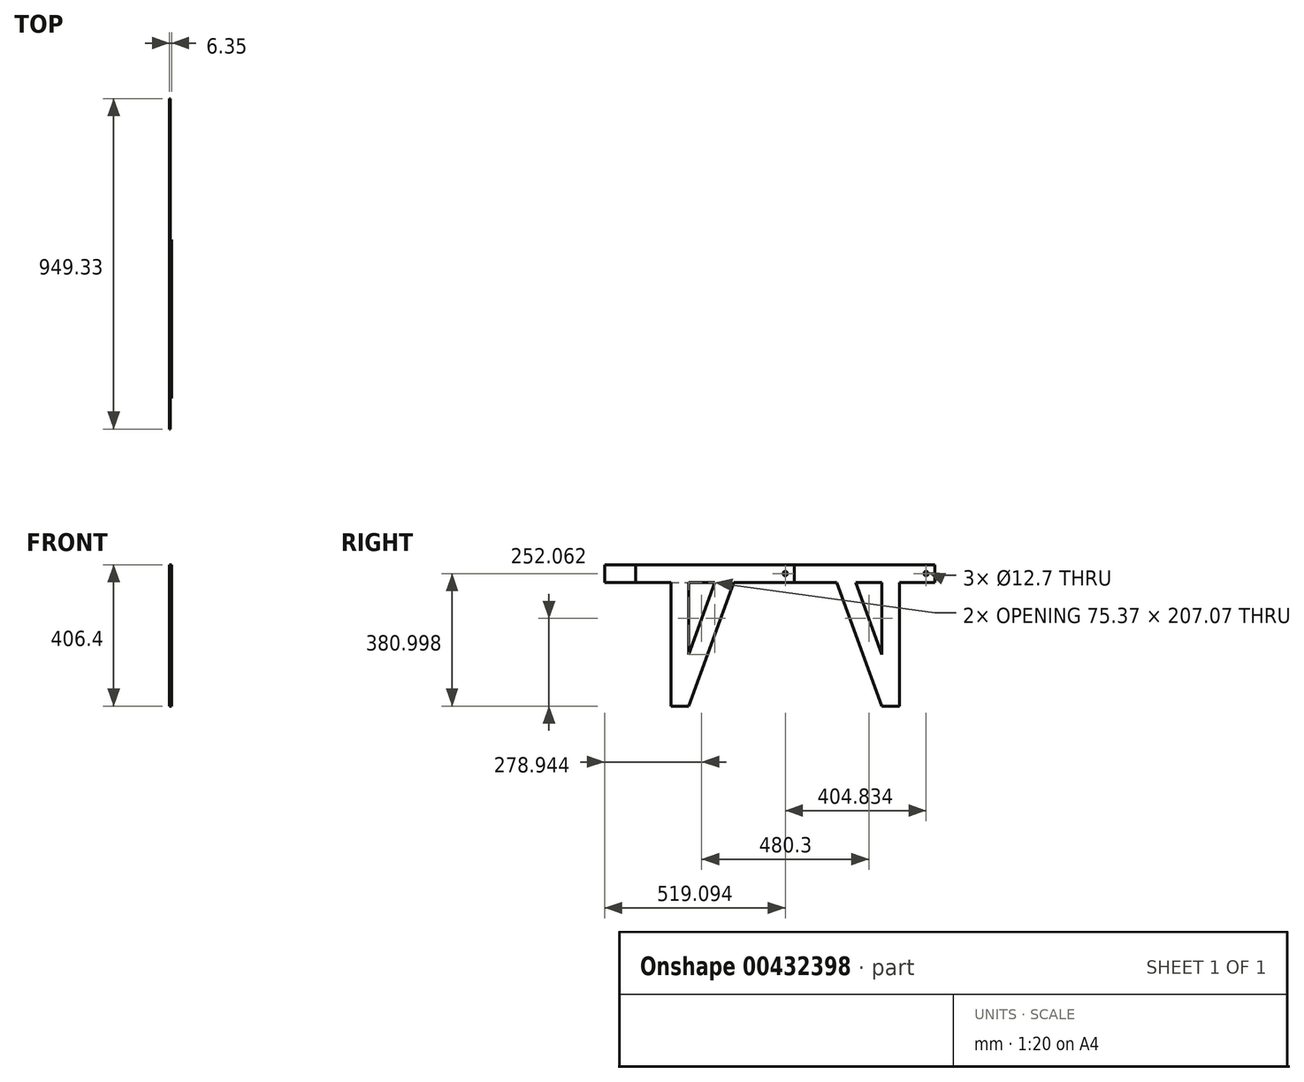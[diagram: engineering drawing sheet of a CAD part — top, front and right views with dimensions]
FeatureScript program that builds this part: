
annotation { "Feature Type Name" : "Feature", "Feature Type Description" : "" }
export const myFeature = defineFeature(function(context is Context, id is Id, definition is map)
    precondition{}
    {
        {
            var Q0;
            Q0=qCreatedBy(makeId("Right.planeOp"),FACE);
            var sketch = newSketch(context, id + "F0", { "sketchPlane" : qUnion([Q0])});
            skLineSegment(sketch, "E0.bottom", {"start": v(-588.96, 209.37) * mm, "end": v(360.37, 209.37) * mm});
            skLineSegment(sketch, "E0.top", {"start": v(-588.96, 158.57) * mm, "end": v(78.54, 158.57) * mm});
            skLineSegment(sketch, "E0.left", {"start": v(-588.96, 209.37) * mm, "end": v(-588.96, 158.57) * mm});
            skLineSegment(sketch, "E0.right", {"start": v(360.37, 209.37) * mm, "end": v(360.37, 158.57) * mm});
            skLineSegment(sketch, "E1.top", {"start": v(207.97, -197.03) * mm, "end": v(258.77, -197.03) * mm});
            skLineSegment(sketch, "E1.left", {"start": v(207.97, 158.57) * mm, "end": v(207.97, -48.5) * mm});
            skLineSegment(sketch, "E1.right", {"start": v(258.77, 158.57) * mm, "end": v(258.77, -197.03) * mm});
            skLineSegment(sketch, "E2.left", {"start": v(78.54, 158.57) * mm, "end": v(207.97, -197.03) * mm});
            skLineSegment(sketch, "E2.right", {"start": v(132.6, 158.57) * mm, "end": v(207.97, -48.5) * mm});
            skLineSegment(sketch, "E3.trimOffspring", {"start": v(132.6, 158.57) * mm, "end": v(207.97, 158.57) * mm});
            skLineSegment(sketch, "E4.trimOffspring", {"start": v(258.77, 158.57) * mm, "end": v(360.37, 158.57) * mm});
            skLineSegment(sketch, "E5", {"start": v(132.6, 158.57) * mm, "end": v(84.86, 141.2) * mm, "construction": true});
            skLineSegment(sketch, "E6", {"start": v(233.37, -197.03) * mm, "end": v(233.37, 183.97) * mm, "construction": true});
            skLineSegment(sketch, "E7", {"start": v(233.37, 183.97) * mm, "end": v(360.37, 183.97) * mm, "construction": true});
            skCircle(sketch, "E8", {"center": v(334.97, 183.97) * mm, "radius": 6.35 * mm});
            skSolve(sketch);
        }
        {
            var Q0;
            Q0=qSketchRegion(id+"F0",true);
            extrude(context, id + "F1", {"entities" : qUnion([Q0]), "depth" : 3.17 * mm});
        }
        {
            var Q0;
            Q0=makeQuery(id+"F1.opExtrude","CAP_FACE",FACE,{"disambiguationData":[OSD([sQuery(id+"F0.wireOp",EDGE,"E0.bottom"),sQuery(id+"F0.wireOp",EDGE,"E0.top"),sQuery(id+"F0.wireOp",EDGE,"E0.left"),sQuery(id+"F0.wireOp",EDGE,"E0.right"),sQuery(id+"F0.wireOp",EDGE,"E1.top"),sQuery(id+"F0.wireOp",EDGE,"E1.left"),sQuery(id+"F0.wireOp",EDGE,"E1.right"),sQuery(id+"F0.wireOp",EDGE,"E2.left"),sQuery(id+"F0.wireOp",EDGE,"E2.right"),sQuery(id+"F0.wireOp",EDGE,"E3.trimOffspring"),sQuery(id+"F0.wireOp",EDGE,"238dff0e-271b-4be5-b624-802031fdb64e.trimOffspring"),sQuery(id+"F0.wireOp",EDGE,"E4.trimOffspring"),sQuery(id+"F0.wireOp",EDGE,"E8")])],"isStart":false});
            var sketch = newSketch(context, id + "F2", { "sketchPlane" : qUnion([Q0])});
            skLineSegment(sketch, "E9", {"start": v(-347.7, -197.03) * mm, "end": v(-398.5, -197.03) * mm});
            skLineSegment(sketch, "E10", {"start": v(-398.5, -197.03) * mm, "end": v(-398.5, 158.57) * mm});
            skLineSegment(sketch, "E11", {"start": v(-398.5, 158.57) * mm, "end": v(-500.1, 158.57) * mm});
            skLineSegment(sketch, "E12", {"start": v(-500.1, 158.57) * mm, "end": v(-500.1, 209.37) * mm});
            skLineSegment(sketch, "E13", {"start": v(-500.1, 209.37) * mm, "end": v(-44.47, 209.37) * mm});
            skLineSegment(sketch, "E14", {"start": v(-44.47, 209.37) * mm, "end": v(-44.47, 158.57) * mm});
            skLineSegment(sketch, "E15", {"start": v(-44.47, 158.57) * mm, "end": v(-218.27, 158.57) * mm});
            skLineSegment(sketch, "E16", {"start": v(-218.27, 158.57) * mm, "end": v(-347.7, -197.03) * mm});
            skLineSegment(sketch, "E17", {"start": v(-347.7, -48.5) * mm, "end": v(-272.33, 158.57) * mm});
            skLineSegment(sketch, "E18", {"start": v(-272.33, 158.57) * mm, "end": v(-347.7, 158.57) * mm});
            skLineSegment(sketch, "E19", {"start": v(-347.7, 158.57) * mm, "end": v(-347.7, -48.5) * mm});
            skLineSegment(sketch, "E20", {"start": v(-272.33, 158.57) * mm, "end": v(-224.6, 141.2) * mm, "construction": true});
            skCircle(sketch, "E21", {"center": v(-69.87, 183.97) * mm, "radius": 6.35 * mm});
            skLineSegment(sketch, "E22", {"start": v(-347.7, -197.03) * mm, "end": v(-69.87, -197.03) * mm, "construction": true});
            skLineSegment(sketch, "E23", {"start": v(-69.87, -197.03) * mm, "end": v(207.97, -197.03) * mm, "construction": true});
            skSolve(sketch);
        }
        {
            var Q0;
            Q0=qSketchRegion(id+"F2",true);
            extrude(context, id + "F3", {"entities" : qUnion([Q0]), "depth" : 3.17 * mm});
        }
        {
            var Q0;
            Q0=makeQuery(id+"F1.opExtrude","CAP_FACE",FACE,{"disambiguationData":[OSD([sQuery(id+"F0.wireOp",EDGE,"E0.bottom"),sQuery(id+"F0.wireOp",EDGE,"E0.top"),sQuery(id+"F0.wireOp",EDGE,"E0.left"),sQuery(id+"F0.wireOp",EDGE,"E0.right"),sQuery(id+"F0.wireOp",EDGE,"E1.top"),sQuery(id+"F0.wireOp",EDGE,"E1.left"),sQuery(id+"F0.wireOp",EDGE,"E1.right"),sQuery(id+"F0.wireOp",EDGE,"E2.left"),sQuery(id+"F0.wireOp",EDGE,"E2.right"),sQuery(id+"F0.wireOp",EDGE,"E3.trimOffspring"),sQuery(id+"F0.wireOp",EDGE,"E4.trimOffspring"),sQuery(id+"F0.wireOp",EDGE,"E8")])],"isStart":false});
            var sketch = newSketch(context, id + "F4", { "sketchPlane" : qUnion([Q0])});
            skCircle(sketch, "E24.0", {"center": v(-69.87, 183.97) * mm, "radius": 6.35 * mm});
            skSolve(sketch);
        }
        {
            var Q0;
            Q0=qSketchRegion(id+"F4",true);
            extrude(context, id + "F5", {"entities" : qUnion([Q0]), "operationType" : NewBodyOperationType.REMOVE, "oppositeDirection" : true, "depth" : 25.4 * mm});
        }
    });
